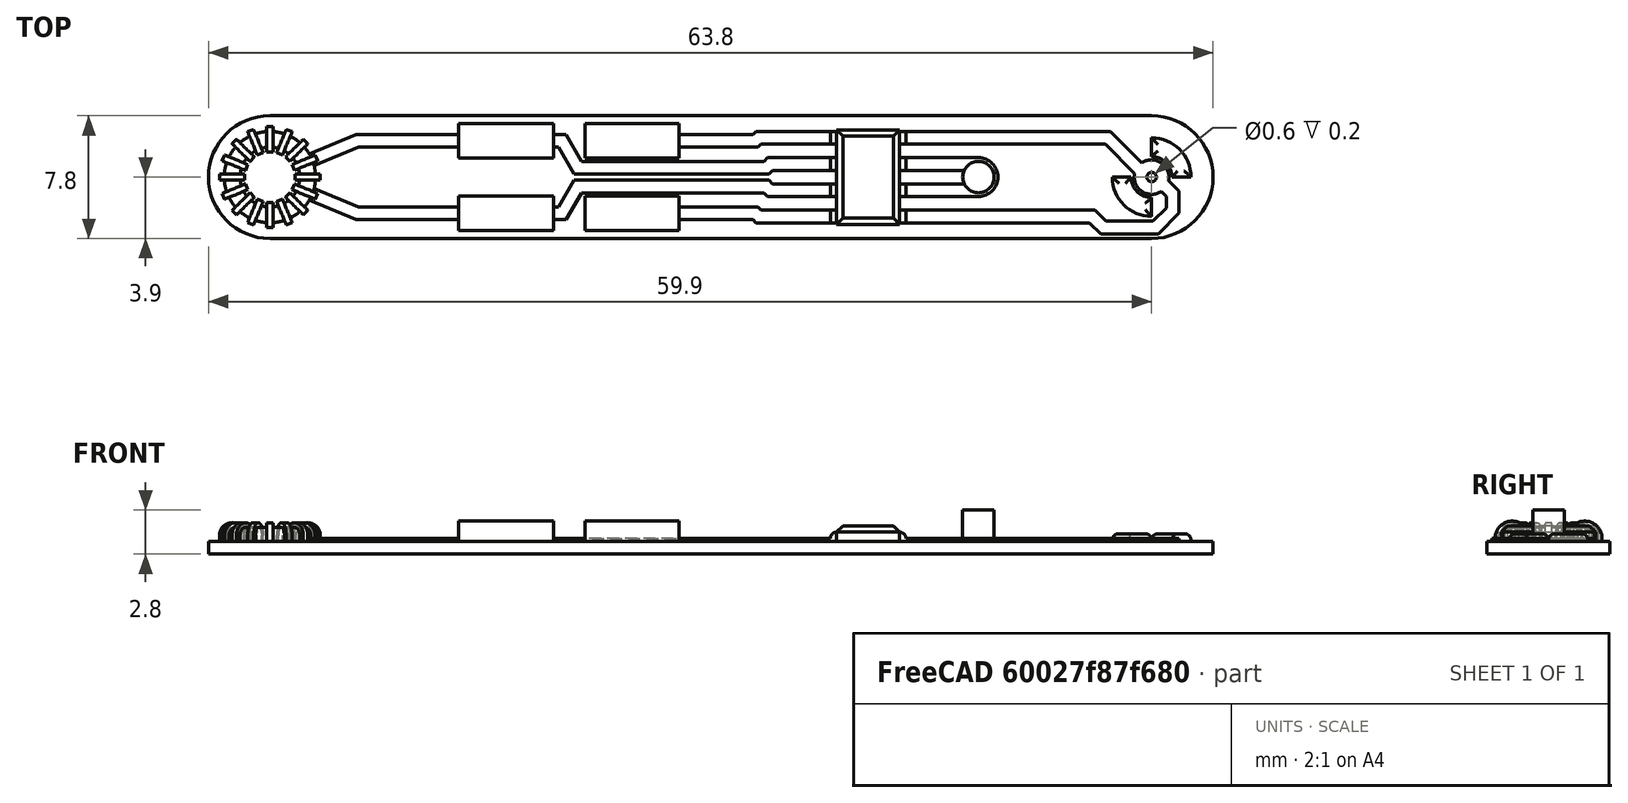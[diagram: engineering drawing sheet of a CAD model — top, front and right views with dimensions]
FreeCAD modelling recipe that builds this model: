
FCSTD DOCUMENT  (FreeCAD 1.0R38641 +678 (Git))
Label: CyberInset
License: All rights reserved
LicenseURL: https://en.wikipedia.org/wiki/All_rights_reserved
objects: Sketcher::SketchObject×15, PartDesign::Pad×13, PartDesign::Plane×3, PartDesign::LinearPattern×3, PartDesign::Revolution×2, PartDesign::Mirrored×2, PartDesign::MultiTransform×2, PartDesign::Fillet×2, PartDesign::PolarPattern×1, PartDesign::Chamfer×1, PartDesign::Body×1, Mesh::Feature×1
note: 104 computed .brp shape members not serialized (recipe doc carries the construction recipe); baked Part::Feature solids carry a one-line shape summary decoded from their .brp

FEATURE [Sketcher::SketchObject] Sketch
  ArcFitTolerance = 1e-06
  AttachmentSupport = -> [XY_Plane]
  FullyConstrained = true
  MakeInternals = false
  MapMode = 5
  sketch-geometry (4):
    g0: ArcOfCircle CenterX=0 CenterY=0 CenterZ=0 NormalX=0 NormalY=0 NormalZ=1 AngleXU=0 Radius=3.9 StartAngle=1.5708 EndAngle=4.71239
    g1: ArcOfCircle CenterX=56 CenterY=-4.1506e-12 CenterZ=0 NormalX=0 NormalY=0 NormalZ=1 AngleXU=0 Radius=3.9 StartAngle=4.71239 EndAngle=7.85398
    g2: LineSegment StartX=2.842e-13 StartY=3.9 StartZ=0 EndX=56 EndY=3.9 EndZ=0
    g3: LineSegment StartX=-1.67279e-11 StartY=-3.9 StartZ=0 EndX=56 EndY=-3.9 EndZ=0
  constraints (9):
    c: Tangent(g0,g2) = 1.5708
    c: Tangent(g0,g3) = -1.5708
    c: Tangent(g1,g2) = 1.5708
    c: Tangent(g1,g3) = -1.5708
    c: Equal(g0,g1)
    c: Horizontal(g3)
    c: DistanceX(g2,g2) = 56
    c: Radius(g0) = 3.9
    c: Coincident(g0,g-1)
FEATURE [PartDesign::Pad] Pad
  Direction = (0,0,1)
  Length = 0.8
  Length2 = 10
  Profile = -> Sketch
  ReferenceAxis = -> Sketch [N_Axis]
  Refine = true
  Reversed = true
  Suppressed = false
  Type = 0
FEATURE [Sketcher::SketchObject] Sketch001
  ArcFitTolerance = 1e-06
  AttachmentSupport = -> [YZ_Plane]
  FullyConstrained = true
  MakeInternals = false
  MapMode = 5
  Placement = pos=(0,0,0) rot=(0.57735,0.57735,0.57735;2.0944rad)
  sketch-geometry (5):
    g0: LineSegment StartX=1.6 StartY=0 StartZ=0 EndX=3.2 EndY=0 EndZ=0
    g1: LineSegment StartX=1.6 StartY=0 StartZ=0 EndX=1.6 EndY=0.4 EndZ=0
    g2: LineSegment StartX=3.2 StartY=0 StartZ=0 EndX=3.2 EndY=0.4 EndZ=0
    g3: LineSegment [constr] StartX=1.6 StartY=0.4 StartZ=0 EndX=3.2 EndY=0.4 EndZ=0
    g4: ArcOfCircle CenterX=2.4 CenterY=0.4 CenterZ=0 NormalX=0 NormalY=0 NormalZ=1 AngleXU=0 Radius=0.8 StartAngle=0 EndAngle=3.14159
  constraints (15):
    c: PointOnObject(g0,g-1)
    c: PointOnObject(g0,g-1)
    c: Coincident(g1,g0)
    c: Vertical(g1)
    c: Coincident(g2,g0)
    c: Vertical(g2)
    c: Coincident(g3,g1)
    c: Coincident(g3,g2)
    c: Horizontal(g3)
    c: Distance(g1,g-2) = 1.6
    c: DistanceX(g3,g3) = 1.6
    c: Distance(g1,g1) = 0.4
    c: Coincident(g4,g1)
    c: Coincident(g4,g2)
    c: PointOnObject(g4,g3)
FEATURE [PartDesign::Pad] Pad001
  BaseFeature = -> Pad
  Direction = (1,0,0)
  Length = 0.2
  Length2 = 0.2
  Profile = -> Sketch001
  ReferenceAxis = -> Sketch001 [N_Axis]
  Refine = true
  Suppressed = false
  Type = 4
FEATURE [Sketcher::SketchObject] Sketch002
  ArcFitTolerance = 1e-06
  AttachmentSupport = -> [YZ_Plane]
  FullyConstrained = true
  MakeInternals = false
  MapMode = 5
  Placement = pos=(0,0,0) rot=(0.57735,0.57735,0.57735;2.0944rad)
  sketch-geometry (5):
    g0: LineSegment StartX=1.9 StartY=0 StartZ=0 EndX=2.9 EndY=0 EndZ=0
    g1: LineSegment StartX=1.9 StartY=0 StartZ=0 EndX=1.9 EndY=0.4 EndZ=0
    g2: LineSegment StartX=2.9 StartY=0 StartZ=0 EndX=2.9 EndY=0.4 EndZ=0
    g3: LineSegment [constr] StartX=1.9 StartY=0.4 StartZ=0 EndX=2.9 EndY=0.4 EndZ=0
    g4: ArcOfCircle CenterX=2.4 CenterY=0.4 CenterZ=0 NormalX=0 NormalY=0 NormalZ=1 AngleXU=0 Radius=0.5 StartAngle=1e-16 EndAngle=3.14159
  constraints (15):
    c: PointOnObject(g0,g-1)
    c: PointOnObject(g0,g-1)
    c: Coincident(g1,g0)
    c: Vertical(g1)
    c: Coincident(g2,g0)
    c: Vertical(g2)
    c: Coincident(g3,g1)
    c: Coincident(g3,g2)
    c: Horizontal(g3)
    c: Coincident(g4,g1)
    c: Coincident(g4,g2)
    c: PointOnObject(g4,g3)
    c: DistanceX(g-1,g0) = 1.9
    c: DistanceX(g3,g3) = 1
    c: DistanceY(g1,g1) = 0.4
FEATURE [PartDesign::Revolution] Revolution
  Angle = 360
  Angle2 = 60
  Axis = (0,0,1)
  Base = (0,0,0)
  BaseFeature = -> Pad001
  Profile = -> Sketch002
  ReferenceAxis = -> Sketch002 [V_Axis]
  Refine = true
  Reversed = true
  Suppressed = false
  Type = 0
FEATURE [PartDesign::PolarPattern] PolarPattern
  Angle = 360
  Axis = -> Z_Axis
  BaseFeature = -> Revolution
  Mode = 0
  Occurrences = 16
  Offset = 120
  Originals = -> [Pad001]
  Refine = true
  Suppressed = false
  TransformMode = 0
FEATURE [Sketcher::SketchObject] Sketch003
  ArcFitTolerance = 1e-06
  AttachmentSupport = -> [PolarPattern]
  FullyConstrained = true
  MakeInternals = false
  MapMode = 5
  sketch-geometry (4):
    g0: LineSegment StartX=36 StartY=3 StartZ=0 EndX=36 EndY=-3 EndZ=0
    g1: LineSegment StartX=36 StartY=-3 StartZ=0 EndX=40 EndY=-3 EndZ=0
    g2: LineSegment StartX=40 StartY=-3 StartZ=0 EndX=40 EndY=3 EndZ=0
    g3: LineSegment StartX=40 StartY=3 StartZ=0 EndX=36 EndY=3 EndZ=0
  constraints (12):
    c: Coincident(g0,g1)
    c: Coincident(g1,g2)
    c: Coincident(g2,g3)
    c: Coincident(g3,g0)
    c: Vertical(g0)
    c: Vertical(g2)
    c: Horizontal(g1)
    c: Horizontal(g3)
    c: Distance(g3,g3) = 4
    c: Distance(g0,g0) = 6
    c: DistanceY(g-1,g0) = 3
    c: DistanceX(g-1,g0) = 36
FEATURE [PartDesign::Pad] Pad002
  BaseFeature = -> PolarPattern
  Direction = (0,0,1)
  Length = 1
  Length2 = 10
  Profile = -> Sketch003
  ReferenceAxis = -> Sketch003 [N_Axis]
  Refine = true
  Suppressed = false
  Type = 0
FEATURE [PartDesign::Chamfer] Chamfer
  Angle = 45
  Base = -> Pad002 [Edge378,Edge376,Edge374,Edge379]
  BaseFeature = -> Pad002
  ChamferType = 0
  FlipDirection = false
  Refine = true
  Size = 0.4
  Size2 = 1
  SupportTransform = false
  Suppressed = false
  UseAllEdges = false
FEATURE [PartDesign::Plane] DatumPlane
  AttachmentOffset = pos=(0,0,-2.9) rot=(0,0,1;0rad)
  AttachmentSupport = -> [XZ_Plane]
  Length = 97.9307
  MapMode = 5
  Placement = pos=(0,2.9,-6e-16) rot=(1,0,0;1.5708rad)
  ResizeMode = 0
  Width = 63.0307
FEATURE [Sketcher::SketchObject] Sketch004
  ArcFitTolerance = 1e-06
  AttachmentSupport = -> [DatumPlane]
  ExternalGeometry = -> [Chamfer]
  FullyConstrained = true
  MakeInternals = false
  MapMode = 5
  Placement = pos=(0,2.9,-6e-16) rot=(1,0,0;1.5708rad)
  sketch-geometry (5):
    g0: LineSegment StartX=36 StartY=0 StartZ=0 EndX=36 EndY=0.6 EndZ=0
    g1: LineSegment StartX=36 StartY=0 StartZ=0 EndX=35.6 EndY=0 EndZ=0
    g2: LineSegment StartX=35.6 StartY=0 StartZ=0 EndX=35.6 EndY=0.2 EndZ=0
    g3: LineSegment [constr] StartX=35.6 StartY=0.2 StartZ=0 EndX=36 EndY=0.2 EndZ=0
    g4: ArcOfCircle CenterX=36 CenterY=0.2 CenterZ=0 NormalX=0 NormalY=0 NormalZ=1 AngleXU=0 Radius=0.4 StartAngle=1.5708 EndAngle=3.14159
  constraints (14):
    c: Coincident(g0,g-3)
    c: Vertical(g0)
    c: Coincident(g1,g0)
    c: PointOnObject(g1,g-1)
    c: Coincident(g2,g1)
    c: Vertical(g2)
    c: Coincident(g3,g2)
    c: PointOnObject(g3,g0)
    c: Horizontal(g3)
    c: Coincident(g4,g3)
    c: Coincident(g4,g2)
    c: Coincident(g4,g0)
    c: DistanceX(g3,g3) = 0.4
    c: DistanceY(g2,g2) = 0.2
FEATURE [PartDesign::Pad] Pad003
  BaseFeature = -> Chamfer
  Direction = (0,-1,2e-16)
  Length = 0.8
  Length2 = 10
  Profile = -> Sketch004
  ReferenceAxis = -> Sketch004 [N_Axis]
  Refine = true
  Suppressed = false
  Type = 0
FEATURE [PartDesign::Plane] DatumPlane001
  AttachmentOffset = pos=(0,0,38) rot=(0,0,1;0rad)
  AttachmentSupport = -> [YZ_Plane]
  Length = 60
  MapMode = 5
  Placement = pos=(38,0,0) rot=(0.57735,0.57735,0.57735;2.0944rad)
  ResizeMode = 0
  Width = 60
FEATURE [PartDesign::Mirrored] Mirrored
  MirrorPlane = -> DatumPlane001
  Refine = true
  Suppressed = false
  TransformMode = 0
FEATURE [PartDesign::LinearPattern] LinearPattern
  Direction = -> Sketch004 [N_Axis]
  Length = 5
  Mode = 0
  Occurrences = 4
  Offset = 1.66667
  Refine = true
  Suppressed = false
  TransformMode = 0
FEATURE [PartDesign::MultiTransform] MultiTransform
  BaseFeature = -> Pad003
  Originals = -> [Pad003]
  Refine = true
  Suppressed = false
  TransformMode = 0
  Transformations = -> [Mirrored,LinearPattern]
FEATURE [Sketcher::SketchObject] Sketch005
  ArcFitTolerance = 1e-06
  AttachmentSupport = -> [MultiTransform]
  FullyConstrained = true
  MakeInternals = false
  MapMode = 5
  sketch-geometry (4):
    g0: LineSegment StartX=12 StartY=3.4 StartZ=0 EndX=12 EndY=1.2 EndZ=0
    g1: LineSegment StartX=12 StartY=1.2 StartZ=0 EndX=18 EndY=1.2 EndZ=0
    g2: LineSegment StartX=18 StartY=1.2 StartZ=0 EndX=18 EndY=3.4 EndZ=0
    g3: LineSegment StartX=18 StartY=3.4 StartZ=0 EndX=12 EndY=3.4 EndZ=0
  constraints (12):
    c: Coincident(g0,g1)
    c: Coincident(g1,g2)
    c: Coincident(g2,g3)
    c: Coincident(g3,g0)
    c: Vertical(g0)
    c: Vertical(g2)
    c: Horizontal(g1)
    c: Horizontal(g3)
    c: DistanceX(g-1,g0) = 12
    c: DistanceX(g3,g3) = 6
    c: DistanceY(g2,g2) = 2.2
    c: DistanceY(g-1,g0) = 1.2
FEATURE [PartDesign::Pad] Pad004
  BaseFeature = -> MultiTransform
  Direction = (0,0,1)
  Length = 0.2
  Length2 = 10
  Profile = -> Sketch005
  ReferenceAxis = -> Sketch005 [N_Axis]
  Refine = true
  Suppressed = false
  Type = 0
FEATURE [Sketcher::SketchObject] Sketch006
  ArcFitTolerance = 1e-06
  AttachmentSupport = -> [Pad004]
  ExternalGeometry = -> [Pad004]
  FullyConstrained = true
  MakeInternals = false
  MapMode = 5
  Placement = pos=(18,0,0) rot=(0.57735,0.57735,0.57735;2.0944rad)
  sketch-geometry (2):
    g0: ArcOfCircle CenterX=2.3 CenterY=0.2 CenterZ=0 NormalX=0 NormalY=0 NormalZ=1 AngleXU=0 Radius=1.1 StartAngle=0 EndAngle=3.14159
    g1: LineSegment StartX=1.2 StartY=0.2 StartZ=0 EndX=3.4 EndY=0.2 EndZ=0
  constraints (5):
    c: Coincident(g1,g-3)
    c: Coincident(g1,g-3)
    c: Coincident(g0,g1)
    c: Coincident(g0,g1)
    c: PointOnObject(g0,g1)
FEATURE [PartDesign::Pad] Pad005
  BaseFeature = -> Pad004
  Direction = (1,0,0)
  Length = 10
  Length2 = 10
  Profile = -> Sketch006
  ReferenceAxis = -> Sketch006 [N_Axis]
  Refine = true
  Reversed = true
  Suppressed = false
  Type = 3
  UpToFace = -> Pad004 [Face108]
FEATURE [PartDesign::LinearPattern] LinearPattern001
  Direction = -> X_Axis
  Length = 8
  Mode = 0
  Occurrences = 2
  Offset = 8
  Refine = true
  Suppressed = false
  TransformMode = 0
FEATURE [PartDesign::LinearPattern] LinearPattern002
  Direction = -> Y_Axis
  Length = 4.6
  Mode = 0
  Occurrences = 2
  Offset = 4.6
  Refine = true
  Reversed = true
  Suppressed = false
  TransformMode = 0
FEATURE [PartDesign::MultiTransform] MultiTransform001
  BaseFeature = -> Pad005
  Originals = -> [Pad004,Pad005]
  Refine = true
  Suppressed = false
  TransformMode = 0
  Transformations = -> [LinearPattern001,LinearPattern002]
FEATURE [PartDesign::Plane] DatumPlane002
  AttachmentOffset = pos=(0,0,56) rot=(0,0,1;0rad)
  AttachmentSupport = -> [YZ_Plane]
  Length = 60
  MapMode = 5
  Placement = pos=(56,0,0) rot=(0.57735,0.57735,0.57735;2.0944rad)
  ResizeMode = 0
  Width = 60
FEATURE [Sketcher::SketchObject] Sketch008
  ArcFitTolerance = 1e-06
  AttachmentSupport = -> [DatumPlane002]
  FullyConstrained = true
  MakeInternals = false
  MapMode = 5
  Placement = pos=(56,0,0) rot=(0.57735,0.57735,0.57735;2.0944rad)
  sketch-geometry (8):
    g0: LineSegment StartX=1.3 StartY=0 StartZ=0 EndX=2.5 EndY=0 EndZ=0
    g1: LineSegment StartX=2.5 StartY=0 StartZ=0 EndX=2.5 EndY=0.5 EndZ=0
    g2: LineSegment StartX=2.5 StartY=0.5 StartZ=0 EndX=1.3 EndY=0.5 EndZ=0
    g3: LineSegment StartX=1.3 StartY=0.5 StartZ=0 EndX=1.3 EndY=0 EndZ=0
    g4: LineSegment StartX=-1.3 StartY=0 StartZ=0 EndX=-1.3 EndY=0.5 EndZ=0
    g5: LineSegment StartX=-1.3 StartY=0.5 StartZ=0 EndX=-2.5 EndY=0.5 EndZ=0
    g6: LineSegment StartX=-2.5 StartY=0.5 StartZ=0 EndX=-2.5 EndY=0 EndZ=0
    g7: LineSegment StartX=-2.5 StartY=0 StartZ=0 EndX=-1.3 EndY=0 EndZ=0
  constraints (24):
    c: Coincident(g0,g1)
    c: Coincident(g1,g2)
    c: Coincident(g2,g3)
    c: Coincident(g3,g0)
    c: Horizontal(g0)
    c: Horizontal(g2)
    c: Vertical(g1)
    c: Vertical(g3)
    c: PointOnObject(g0,g-1)
    c: Coincident(g4,g5)
    c: Coincident(g5,g6)
    c: Coincident(g6,g7)
    c: Coincident(g7,g4)
    c: Vertical(g4)
    c: Vertical(g6)
    c: Horizontal(g5)
    c: Horizontal(g7)
    c: PointOnObject(g4,g-1)
    c: Equal(g5,g2)
    c: Equal(g6,g3)
    c: DistanceX(g-1,g0) = 1.3
    c: DistanceX(g4,g-1) = 1.3
    c: DistanceX(g5,g5) = 1.2
    c: DistanceY(g6,g6) = 0.5
FEATURE [PartDesign::Revolution] Revolution001
  Angle = 90
  Angle2 = 60
  Axis = (0,0,1)
  Base = (56,0,0)
  BaseFeature = -> MultiTransform001
  Profile = -> Sketch008
  ReferenceAxis = -> Sketch008 [V_Axis]
  Refine = true
  Reversed = true
  Suppressed = false
  Type = 0
FEATURE [PartDesign::Fillet] Fillet
  Base = -> Revolution001 [Edge505,Edge509,Edge510,Edge512]
  BaseFeature = -> Revolution001
  Radius = 0.4
  Refine = true
  SupportTransform = false
  Suppressed = false
  UseAllEdges = false
FEATURE [PartDesign::Fillet] Fillet001
  Base = -> Fillet [Edge500,Edge502,Edge504,Edge497]
  BaseFeature = -> Fillet
  Radius = 0.4
  Refine = true
  SupportTransform = false
  Suppressed = false
  UseAllEdges = false
FEATURE [Sketcher::SketchObject] Sketch009
  ArcFitTolerance = 1e-06
  AttachmentSupport = -> [Fillet001]
  FullyConstrained = true
  MakeInternals = false
  MapMode = 5
  sketch-geometry (2):
    g0: Circle CenterX=56 CenterY=0 CenterZ=0 NormalX=0 NormalY=0 NormalZ=1 AngleXU=0 Radius=1.1
    g1: Circle CenterX=56 CenterY=0 CenterZ=0 NormalX=0 NormalY=0 NormalZ=1 AngleXU=0 Radius=0.3
  constraints (5):
    c: PointOnObject(g0,g-1)
    c: Coincident(g1,g0)
    c: DistanceX(g-1,g0) = 56
    c: Diameter(g0) = 2.2
    c: Diameter(g1) = 0.6
FEATURE [PartDesign::Pad] Pad006
  BaseFeature = -> Fillet001
  Direction = (0,0,1)
  Length = 0.2
  Length2 = 10
  Profile = -> Sketch009
  ReferenceAxis = -> Sketch009 [N_Axis]
  Refine = true
  Suppressed = false
  Type = 0
FEATURE [Sketcher::SketchObject] Sketch010
  ArcFitTolerance = 1e-06
  AttachmentSupport = -> [Pad006]
  ExternalGeometry = -> [Pad006]
  FullyConstrained = true
  MakeInternals = false
  MapMode = 5
  sketch-geometry (24):
    g0: Circle [constr] CenterX=56 CenterY=0 CenterZ=0 NormalX=0 NormalY=0 NormalZ=1 AngleXU=0 Radius=3.1
    g1: LineSegment [constr] StartX=53.808 StartY=2.19203 StartZ=0 EndX=58.192 EndY=-2.19203 EndZ=0
    g2: LineSegment [constr] StartX=56 StartY=0 StartZ=0 EndX=56 EndY=3.1 EndZ=0
    g3: LineSegment StartX=56.4243 StartY=-0.707107 StartZ=0 EndX=56.9899 EndY=-0.141421 EndZ=0
    g4: LineSegment StartX=56.9899 StartY=-0.141421 StartZ=0 EndX=57.7399 EndY=-0.891421 EndZ=0
    g5: LineSegment StartX=56.4243 StartY=-0.707107 StartZ=0 EndX=56.9399 EndY=-1.22279 EndZ=0
    g6: LineSegment StartX=57.7399 StartY=-0.891421 StartZ=0 EndX=57.7399 EndY=-2.29142 EndZ=0
    g7: LineSegment StartX=56.9399 StartY=-1.22279 StartZ=0 EndX=56.9399 EndY=-1.96005 EndZ=0
    g8: LineSegment StartX=56.9399 StartY=-1.96005 StartZ=0 EndX=56.1 EndY=-2.8 EndZ=0
    g9: LineSegment StartX=57.7399 StartY=-2.29142 StartZ=0 EndX=56.4314 EndY=-3.6 EndZ=0
    g10: LineSegment StartX=56.1 StartY=-2.8 StartZ=0 EndX=53.1 EndY=-2.8 EndZ=0
    g11: LineSegment StartX=56.4314 StartY=-3.6 StartZ=0 EndX=52.7686 EndY=-3.6 EndZ=0
    g12: LineSegment StartX=53.1 StartY=-2.8 StartZ=0 EndX=52.4 EndY=-2.1 EndZ=0
    g13: LineSegment StartX=52.7686 StartY=-3.6 StartZ=0 EndX=52.0686 EndY=-2.9 EndZ=0
    g14: LineSegment StartX=52.4 StartY=-2.1 StartZ=0 EndX=40.4 EndY=-2.1 EndZ=0
    g15: LineSegment StartX=40.4 StartY=-2.1 StartZ=0 EndX=40.4 EndY=-2.9 EndZ=0
    g16: LineSegment StartX=40.4 StartY=-2.9 StartZ=0 EndX=52.0686 EndY=-2.9 EndZ=0
    g17: LineSegment [constr] StartX=53.808 StartY=-2.19203 StartZ=0 EndX=58.192 EndY=2.19203 EndZ=0
    g18: LineSegment StartX=55.0101 StartY=0.141421 StartZ=0 EndX=55.5757 EndY=0.707107 EndZ=0
    g19: LineSegment StartX=55.5757 StartY=0.707107 StartZ=0 EndX=53.3828 EndY=2.9 EndZ=0
    g20: LineSegment StartX=53.3828 StartY=2.9 StartZ=0 EndX=40.4 EndY=2.9 EndZ=0
    g21: LineSegment StartX=40.4 StartY=2.9 StartZ=0 EndX=40.4 EndY=2.1 EndZ=0
    g22: LineSegment StartX=40.4 StartY=2.1 StartZ=0 EndX=53.0515 EndY=2.1 EndZ=0
    g23: LineSegment StartX=53.0515 StartY=2.1 StartZ=0 EndX=55.0101 EndY=0.141421 EndZ=0
  constraints (70):
    c: PointOnObject(g0,g-1)
    c: DistanceX(g-1,g0) = 56
    c: PointOnObject(g1,g0)
    c: PointOnObject(g1,g0)
    c: PointOnObject(g0,g1)
    c: Coincident(g2,g0)
    c: PointOnObject(g2,g0)
    c: Vertical(g2)
    c: Angle(g2,g1) = 0.785398
    c: Diameter(g0) = 6.2
    c: Coincident(g4,g3)
    c: Coincident(g5,g3)
    c: Coincident(g6,g4)
    c: Coincident(g7,g5)
    c: Vertical(g7)
    c: Coincident(g8,g7)
    c: Coincident(g9,g6)
    c: Coincident(g10,g8)
    c: Horizontal(g10)
    c: Coincident(g11,g9)
    c: Horizontal(g11)
    c: Coincident(g12,g10)
    c: Coincident(g13,g11)
    c: Coincident(g14,g12)
    c: Horizontal(g14)
    c: Coincident(g15,g14)
    c: Coincident(g16,g15)
    c: Coincident(g16,g13)
    c: Horizontal(g16)
    c: Parallel(g5,g1)
    c: Parallel(g4,g1)
    c: Perpendicular(g4,g3)
    c: Vertical(g6)
    c: Distance(g4,g5) = 0.8
    c: Distance(g5,g1) = 0.2
    c: Coincident(g15,g-3)
    c: Coincident(g14,g-3)
    c: Parallel(g12,g1)
    c: Parallel(g12,g13)
    c: Distance(g6,g7) = 0.8
    c: Perpendicular(g1,g8)
    c: Parallel(g9,g8)
    c: Distance(g9,g8) = 0.8
    c: Distance(g11,g10) = 0.8
    c: Distance(g12,g13) = 0.8
    c: PointOnObject(g17,g0)
    c: PointOnObject(g17,g0)
    c: PointOnObject(g0,g17)
    c: Perpendicular(g1,g17)
    c: Distance(g17,g3) = 0.8
    c: DistanceX(g14,g14) = 12
    c: DistanceX(g10,g10) = 3
    c: DistanceY(g6,g6) = 1.4
    c: Coincident(g19,g18)
    c: Coincident(g20,g19)
    c: Horizontal(g20)
    c: Coincident(g21,g20)
    c: Coincident(g22,g21)
    c: Horizontal(g22)
    c: Coincident(g23,g22)
    c: Coincident(g23,g18)
    c: Coincident(g20,g-4)
    c: Coincident(g21,g-4)
    c: Parallel(g23,g1)
    c: Parallel(g19,g1)
    c: Perpendicular(g23,g18)
    c: Distance(g23,g1) = 0.6
    c: Distance(g19,g1) = 0.2
    c: Distance(g17,g18) = 0.8
    c: Distance(g10,g-1) = 2.8
FEATURE [PartDesign::Pad] Pad007
  BaseFeature = -> Pad006
  Direction = (0,0,1)
  Length = 0.2
  Length2 = 10
  Profile = -> Sketch010
  ReferenceAxis = -> Sketch010 [N_Axis]
  Refine = true
  Suppressed = false
  Type = 0
FEATURE [Sketcher::SketchObject] Sketch011
  ArcFitTolerance = 1e-06
  AttachmentSupport = -> [Pad007]
  FullyConstrained = true
  MakeInternals = false
  MapMode = 5
  sketch-geometry (1):
    g0: Circle CenterX=45 CenterY=0 CenterZ=0 NormalX=0 NormalY=0 NormalZ=1 AngleXU=0 Radius=1
  constraints (3):
    c: PointOnObject(g0,g-1)
    c: Diameter(g0) = 2
    c: DistanceX(g-1,g0) = 45
FEATURE [PartDesign::Pad] Pad008
  BaseFeature = -> Pad007
  Direction = (0,0,1)
  Length = 2
  Length2 = 10
  Profile = -> Sketch011
  ReferenceAxis = -> Sketch011 [N_Axis]
  Refine = true
  Suppressed = false
  Type = 0
FEATURE [Sketcher::SketchObject] Sketch012
  ArcFitTolerance = 1e-06
  AttachmentSupport = -> [Pad008]
  ExternalGeometry = -> [Pad008]
  FullyConstrained = true
  MakeInternals = false
  MapMode = 5
  sketch-geometry (9):
    g0: LineSegment StartX=40.4 StartY=1.23333 StartZ=0 EndX=40.4 EndY=0.433333 EndZ=0
    g1: LineSegment StartX=40.4 StartY=0.433333 StartZ=0 EndX=45 EndY=0.433333 EndZ=0
    g2: LineSegment StartX=40.4 StartY=1.23333 StartZ=0 EndX=45 EndY=1.23333 EndZ=0
    g3: LineSegment StartX=40.4 StartY=-1.23333 StartZ=0 EndX=45 EndY=-1.23333 EndZ=0
    g4: LineSegment StartX=40.4 StartY=-0.433333 StartZ=0 EndX=45 EndY=-0.433333 EndZ=0
    g5: LineSegment [constr] StartX=45 StartY=1.23333 StartZ=0 EndX=45 EndY=-1.23333 EndZ=0
    g6: ArcOfCircle CenterX=45 CenterY=-2e-16 CenterZ=0 NormalX=0 NormalY=0 NormalZ=1 AngleXU=0 Radius=1.23333 StartAngle=4.71239 EndAngle=7.85398
    g7: ArcOfCircle CenterX=45 CenterY=-2e-16 CenterZ=0 NormalX=0 NormalY=0 NormalZ=1 AngleXU=0 Radius=0.433333 StartAngle=4.71239 EndAngle=7.85398
    g8: LineSegment StartX=40.4 StartY=-0.433333 StartZ=0 EndX=40.4 EndY=-1.23333 EndZ=0
  constraints (24):
    c: Coincident(g0,g-3)
    c: Coincident(g0,g-3)
    c: Coincident(g1,g0)
    c: Horizontal(g1)
    c: Coincident(g2,g0)
    c: Horizontal(g2)
    c: Coincident(g3,g-4)
    c: Horizontal(g3)
    c: Coincident(g4,g-4)
    c: Horizontal(g4)
    c: Coincident(g5,g2)
    c: Coincident(g5,g3)
    c: Vertical(g5)
    c: PointOnObject(g1,g5)
    c: PointOnObject(g4,g5)
    c: PointOnObject(g6,g5)
    c: Coincident(g6,g2)
    c: Coincident(g6,g3)
    c: PointOnObject(g7,g5)
    c: Coincident(g7,g1)
    c: Coincident(g7,g4)
    c: Distance(g3,g-2) = 45
    c: Coincident(g8,g4)
    c: Coincident(g8,g3)
FEATURE [PartDesign::Pad] Pad009
  BaseFeature = -> Pad008
  Direction = (0,0,1)
  Length = 0.2
  Length2 = 10
  Profile = -> Sketch012
  ReferenceAxis = -> Sketch012 [N_Axis]
  Refine = true
  Suppressed = false
  Type = 0
FEATURE [Sketcher::SketchObject] Sketch013
  ArcFitTolerance = 1e-06
  AttachmentSupport = -> [Pad009]
  ExternalGeometry = -> [Pad009]
  FullyConstrained = true
  MakeInternals = false
  MapMode = 5
  sketch-geometry (8):
    g0: LineSegment StartX=26 StartY=-1.9 StartZ=0 EndX=26 EndY=-2.7 EndZ=0
    g1: LineSegment StartX=26 StartY=-1.9 StartZ=0 EndX=31 EndY=-1.9 EndZ=0
    g2: LineSegment StartX=26 StartY=-2.7 StartZ=0 EndX=30.6686 EndY=-2.7 EndZ=0
    g3: LineSegment StartX=30.6686 StartY=-2.7 StartZ=0 EndX=30.8686 EndY=-2.9 EndZ=0
    g4: LineSegment StartX=31 StartY=-1.9 StartZ=0 EndX=31.2 EndY=-2.1 EndZ=0
    g5: LineSegment StartX=35.6 StartY=-2.1 StartZ=0 EndX=31.2 EndY=-2.1 EndZ=0
    g6: LineSegment StartX=35.6 StartY=-2.9 StartZ=0 EndX=30.8686 EndY=-2.9 EndZ=0
    g7: LineSegment StartX=35.6 StartY=-2.1 StartZ=0 EndX=35.6 EndY=-2.9 EndZ=0
  constraints (22):
    c: PointOnObject(g0,g-3)
    c: PointOnObject(g0,g-3)
    c: Coincident(g1,g0)
    c: Horizontal(g1)
    c: Coincident(g2,g0)
    c: Horizontal(g2)
    c: Coincident(g3,g2)
    c: Coincident(g4,g1)
    c: Coincident(g5,g-4)
    c: Coincident(g5,g4)
    c: Horizontal(g5)
    c: Coincident(g6,g-4)
    c: Coincident(g6,g3)
    c: Horizontal(g6)
    c: Coincident(g7,g5)
    c: Coincident(g7,g6)
    c: Parallel(g3,g4)
    c: Distance(g3,g4) = 0.8
    c: Distance(g0,g0) = 0.8
    c: Angle(g2,g3) = 2.35619
    c: Distance(g1,g-1) = 1.9
    c: DistanceX(g1,g1) = 5
FEATURE [PartDesign::Pad] Pad010
  BaseFeature = -> Pad009
  Direction = (0,0,1)
  Length = 0.2
  Length2 = 10
  Profile = -> Sketch013
  ReferenceAxis = -> Sketch013 [N_Axis]
  Refine = true
  Suppressed = false
  Type = 0
FEATURE [Sketcher::SketchObject] Sketch014
  ArcFitTolerance = 1e-06
  AttachmentSupport = -> [Pad010]
  ExternalGeometry = -> [Pad010]
  FullyConstrained = true
  MakeInternals = false
  MapMode = 5
  sketch-geometry (12):
    g0: LineSegment StartX=18 StartY=-2.7 StartZ=0 EndX=18 EndY=-1.9 EndZ=0
    g1: LineSegment StartX=18 StartY=-1.9 StartZ=0 EndX=18.3381 EndY=-1.9 EndZ=0
    g2: LineSegment StartX=18 StartY=-2.7 StartZ=0 EndX=18.8 EndY=-2.7 EndZ=0
    g3: LineSegment StartX=18.3381 StartY=-1.9 StartZ=0 EndX=19.3196 EndY=-0.2 EndZ=0
    g4: LineSegment StartX=19.3196 StartY=-0.2 StartZ=0 EndX=31.698 EndY=-0.2 EndZ=0
    g5: LineSegment StartX=31.698 StartY=-0.2 StartZ=0 EndX=31.9314 EndY=-0.433333 EndZ=0
    g6: LineSegment StartX=31.9314 StartY=-0.433333 StartZ=0 EndX=35.6 EndY=-0.433333 EndZ=0
    g7: LineSegment StartX=35.6 StartY=-0.433333 StartZ=0 EndX=35.6 EndY=-1.23333 EndZ=0
    g8: LineSegment StartX=35.6 StartY=-1.23333 StartZ=0 EndX=31.6 EndY=-1.23333 EndZ=0
    g9: LineSegment StartX=31.6 StartY=-1.23333 StartZ=0 EndX=31.3667 EndY=-1 EndZ=0
    g10: LineSegment StartX=31.3667 StartY=-1 StartZ=0 EndX=19.7815 EndY=-1 EndZ=0
    g11: LineSegment StartX=19.7815 StartY=-1 StartZ=0 EndX=18.8 EndY=-2.7 EndZ=0
  constraints (34):
    c: PointOnObject(g0,g-3)
    c: PointOnObject(g0,g-3)
    c: Coincident(g1,g0)
    c: Horizontal(g1)
    c: Coincident(g2,g0)
    c: Horizontal(g2)
    c: Coincident(g3,g1)
    c: Coincident(g4,g3)
    c: Horizontal(g4)
    c: Coincident(g5,g4)
    c: Coincident(g6,g5)
    c: Coincident(g6,g-4)
    c: Horizontal(g6)
    c: Coincident(g7,g6)
    c: Coincident(g7,g-4)
    c: Coincident(g8,g7)
    c: Horizontal(g8)
    c: Coincident(g9,g8)
    c: Coincident(g10,g9)
    c: Horizontal(g10)
    c: Coincident(g11,g10)
    c: Coincident(g11,g2)
    c: Parallel(g9,g5)
    c: Angle(g6,g5) = 2.35619
    c: Distance(g10,g4) = 0.8
    c: Distance(g9,g5) = 0.8
    c: Angle(g2,g11) = 1.0472
    c: Parallel(g3,g11)
    c: Distance(g11,g3) = 0.8
    c: Distance(g2,g1) = 0.8
    c: Distance(g0,g-1) = 1.9
    c: Distance(g2,g2) = 0.8
    c: DistanceX(g8,g8) = 4
    c: Distance(g4,g-1) = 0.2
FEATURE [PartDesign::Pad] Pad011
  BaseFeature = -> Pad010
  Direction = (0,0,1)
  Length = 0.2
  Length2 = 10
  Profile = -> Sketch014
  ReferenceAxis = -> Sketch014 [N_Axis]
  Refine = true
  Suppressed = false
  Type = 0
FEATURE [Sketcher::SketchObject] Sketch015
  ArcFitTolerance = 1e-06
  AttachmentSupport = -> [Pad011]
  ExternalGeometry = -> [Pad011]
  FullyConstrained = true
  MakeInternals = false
  MapMode = 5
  sketch-geometry (6):
    g0: LineSegment StartX=12 StartY=-1.9 StartZ=0 EndX=12 EndY=-2.7 EndZ=0
    g1: LineSegment StartX=12 StartY=-1.9 StartZ=0 EndX=5.63226 EndY=-1.9 EndZ=0
    g2: LineSegment StartX=5.47313 StartY=-2.7 StartZ=0 EndX=12 EndY=-2.7 EndZ=0
    g3: LineSegment StartX=5.63226 StartY=-1.9 StartZ=0 EndX=2.63808 EndY=-0.659773 EndZ=0
    g4: LineSegment StartX=2.63808 StartY=-0.659773 StartZ=0 EndX=2.33194 EndY=-1.39888 EndZ=0
    g5: LineSegment StartX=2.33194 StartY=-1.39888 StartZ=0 EndX=5.47313 EndY=-2.7 EndZ=0
  constraints (18):
    c: PointOnObject(g0,g-3)
    c: PointOnObject(g0,g-3)
    c: Coincident(g1,g0)
    c: Coincident(g2,g0)
    c: Horizontal(g1)
    c: Horizontal(g2)
    c: DistanceY(g0,g0) = 0.8
    c: Distance(g1,g-1) = 1.9
    c: Coincident(g3,g1)
    c: Coincident(g4,g3)
    c: Coincident(g5,g4)
    c: Coincident(g5,g2)
    c: Parallel(g5,g3)
    c: Perpendicular(g5,g4)
    c: Distance(g4,g4) = 0.8
    c: Parallel(g-4,g5)
    c: Distance(g-4,g5) = 0.2
    c: Distance(g5,g5) = 3.4
FEATURE [PartDesign::Pad] Pad012
  BaseFeature = -> Pad011
  Direction = (0,0,1)
  Length = 0.2
  Length2 = 10
  Profile = -> Sketch015
  ReferenceAxis = -> Sketch015 [N_Axis]
  Refine = true
  Suppressed = false
  Type = 0
FEATURE [PartDesign::Mirrored] Mirrored001  label="CyberInset"
  BaseFeature = -> Pad012
  MirrorPlane = -> XZ_Plane
  Originals = -> [Pad012,Pad011,Pad010]
  Refine = true
  Suppressed = false
  TransformMode = 0
FEATURE [PartDesign::Body] Body
  AllowCompound = false
  Group = -> [Sketch,Pad,Sketch001,Pad001,Sketch002,Revolution,PolarPattern,Sketch003,Pad002,Chamfer,DatumPlane,Sketch004,Pad003,DatumPlane001,MultiTransform,Mirrored,LinearPattern,Sketch005,Pad004,Sketch006,Pad005,MultiTransform001,LinearPattern001,LinearPattern002,DatumPlane002,Sketch008,Revolution001,Fillet,Fillet001,Sketch009,Pad006,Sketch010,Pad007,Sketch011,Pad008,Sketch012,Pad009,Sketch013,Pad010,+5 more]
  Origin = -> Origin
  Tip = -> Mirrored001
FEATURE [Mesh::Feature] Mesh  label="CyberInset (Meshed)"
